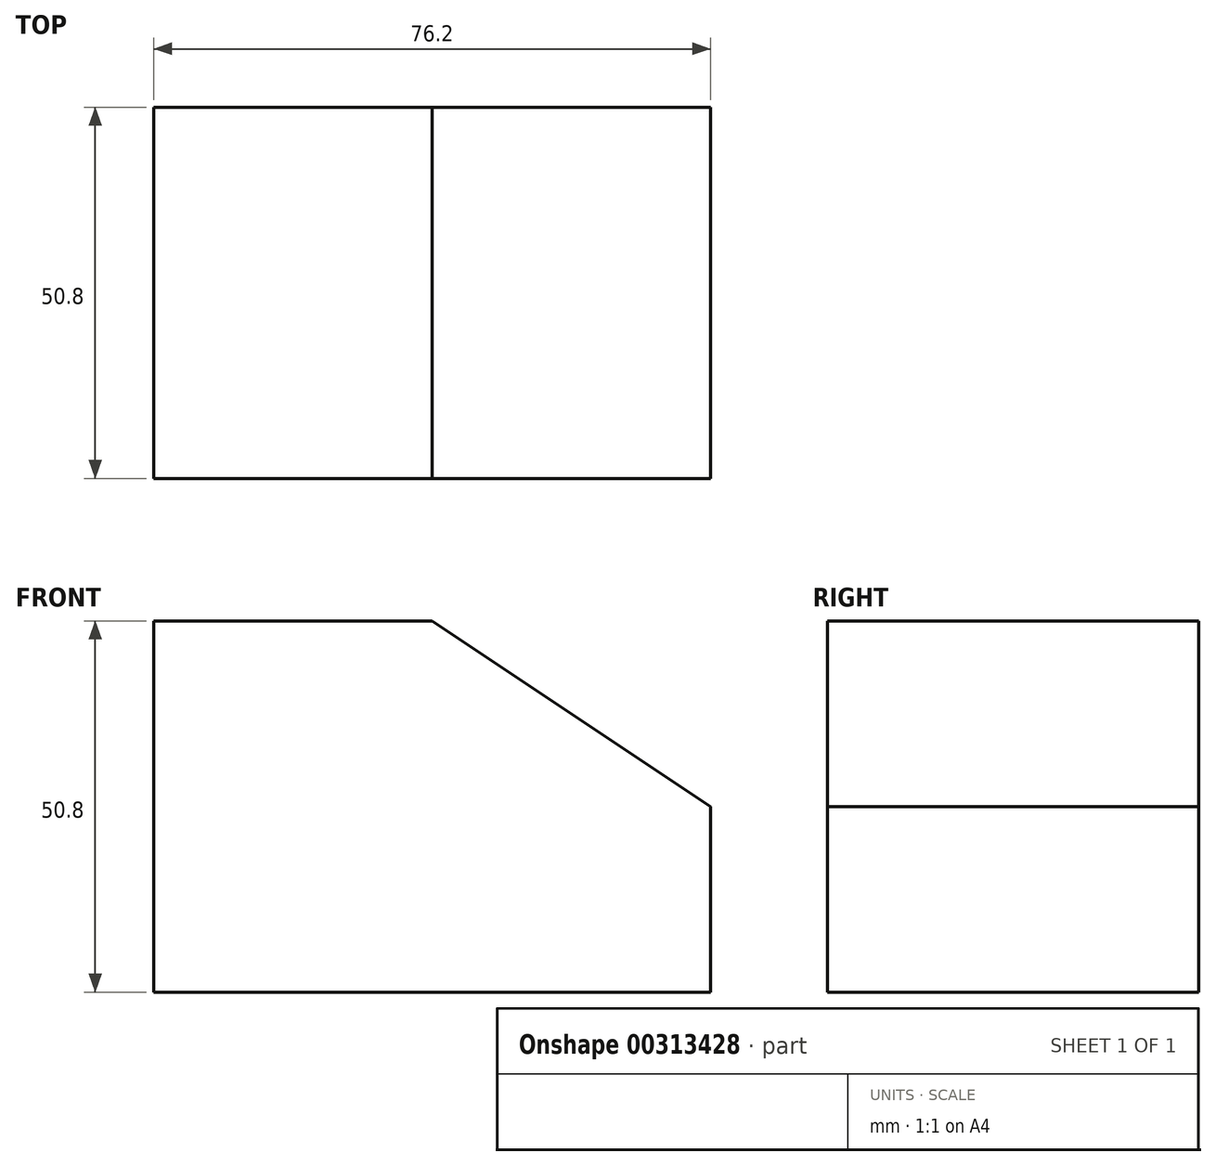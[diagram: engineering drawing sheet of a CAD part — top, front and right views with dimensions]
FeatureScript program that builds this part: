
annotation { "Feature Type Name" : "Feature", "Feature Type Description" : "" }
export const myFeature = defineFeature(function(context is Context, id is Id, definition is map)
    precondition{}
    {
        {
            var Q0;
            Q0=qCreatedBy(makeId("Front.planeOp"),FACE);
            var sketch = newSketch(context, id + "F0", { "sketchPlane" : qUnion([Q0])});
            skLineSegment(sketch, "E0", {"start": v(-45.96, -14.96) * mm, "end": v(30.24, -14.96) * mm});
            skLineSegment(sketch, "E1", {"start": v(-45.96, -14.96) * mm, "end": v(-45.96, 35.84) * mm});
            skLineSegment(sketch, "E2", {"start": v(-45.96, 35.84) * mm, "end": v(-7.86, 35.84) * mm});
            skLineSegment(sketch, "E3", {"start": v(30.24, -14.96) * mm, "end": v(30.24, 10.44) * mm});
            skLineSegment(sketch, "E4", {"start": v(30.24, 10.44) * mm, "end": v(-7.86, 35.84) * mm});
            skSolve(sketch);
        }
        {
            var Q0;
            Q0=makeQuery(id+"F0.imprint","IMPRINT",FACE,{"disambiguationData":[TD([[makeQuery(id+"F0.imprint","IMPRINT",EDGE,{"derivedFrom":sQuery(id+"F0.wireOp",EDGE,"E0")}),1.0]])]});
            extrude(context, id + "F1", {"entities" : qUnion([Q0]), "depth" : 50.8 * mm});
        }
    });
